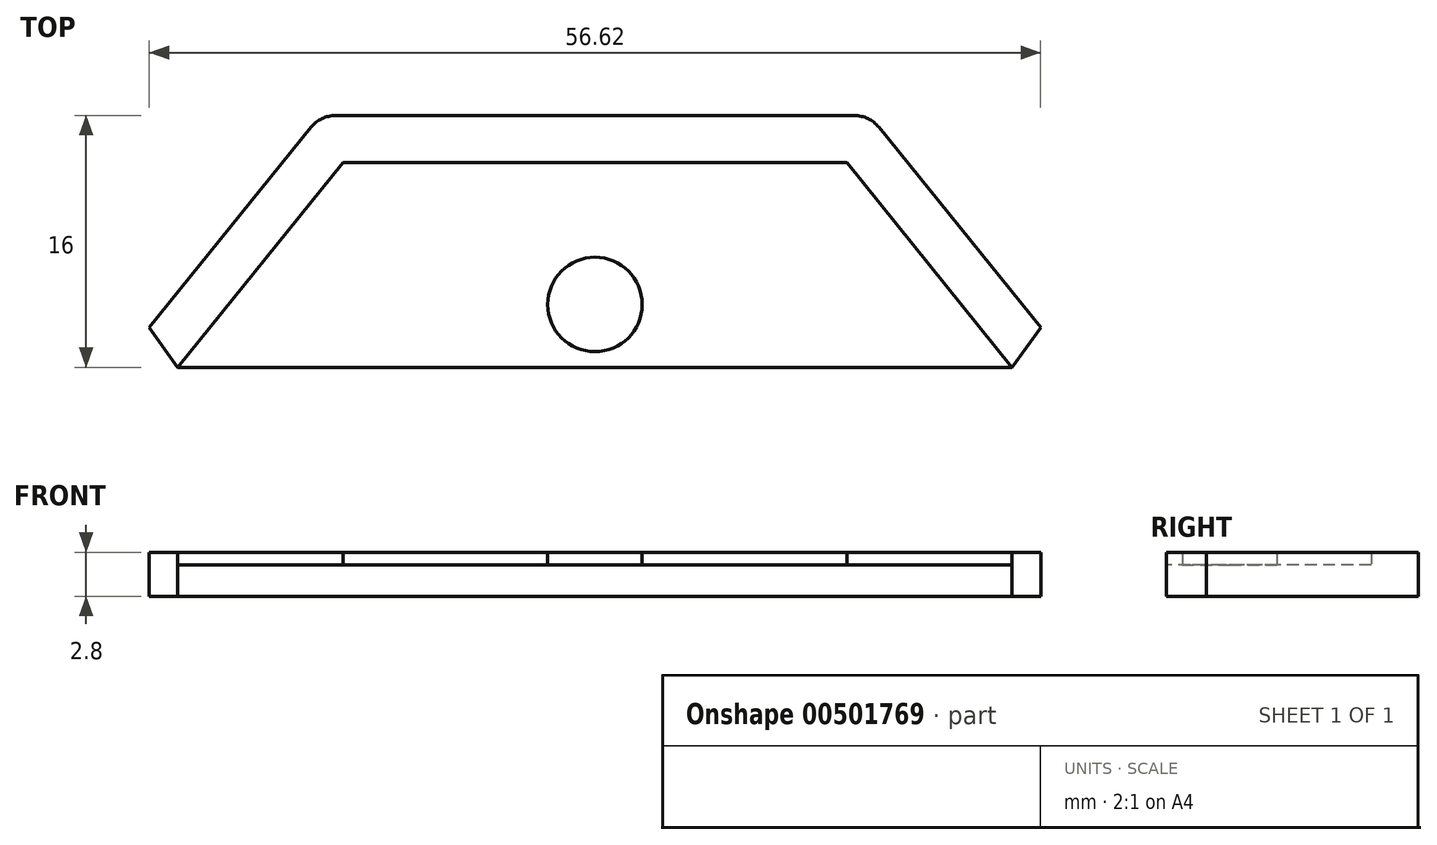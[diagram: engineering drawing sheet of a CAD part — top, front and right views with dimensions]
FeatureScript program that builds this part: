
annotation { "Feature Type Name" : "Feature", "Feature Type Description" : "" }
export const myFeature = defineFeature(function(context is Context, id is Id, definition is map)
    precondition{}
    {
        {
            var Q0;
            Q0=qCreatedBy(makeId("Top.planeOp"),FACE);
            var sketch = newSketch(context, id + "F0", { "sketchPlane" : qUnion([Q0])});
            skLineSegment(sketch, "E0", {"start": v(0, 17.14) * mm, "end": v(0, -16.93) * mm, "construction": true});
            skLineSegment(sketch, "E1", {"start": v(0, 10.35) * mm, "end": v(2, 10.35) * mm});
            skLineSegment(sketch, "E2", {"start": v(-4.02, 1.35) * mm, "end": v(4.37, 1.35) * mm, "construction": true});
            skLineSegment(sketch, "E3", {"start": v(16, 10.35) * mm, "end": v(26.5, -2.65) * mm});
            skLineSegment(sketch, "E4.0", {"start": v(18.03, 12.6) * mm, "end": v(28.31, -0.12) * mm});
            skLineSegment(sketch, "E4.1", {"start": v(0, 13.35) * mm, "end": v(16.48, 13.35) * mm});
            skLineSegment(sketch, "E5", {"start": v(26.5, -2.65) * mm, "end": v(28.31, -0.12) * mm});
            skLineSegment(sketch, "E6.trimOffspring", {"start": v(5.55, 10.35) * mm, "end": v(16, 10.35) * mm});
            skLineSegment(sketch, "E7.MirrorCS", {"start": v(0, 10.35) * mm, "end": v(-2, 10.35) * mm});
            skLineSegment(sketch, "E8.MirrorCS", {"start": v(-18.03, 12.6) * mm, "end": v(-28.31, -0.12) * mm});
            skLineSegment(sketch, "E9.MirrorCS", {"start": v(0, 13.35) * mm, "end": v(-16.48, 13.35) * mm});
            skLineSegment(sketch, "E10.MirrorCS", {"start": v(-26.5, -2.65) * mm, "end": v(-28.31, -0.12) * mm});
            skLineSegment(sketch, "E11.MirrorCS", {"start": v(-5.55, 10.35) * mm, "end": v(-16, 10.35) * mm});
            skLineSegment(sketch, "E12.MirrorCS", {"start": v(-16, 10.35) * mm, "end": v(-26.5, -2.65) * mm});
            skPoint(sketch, "E13.visualSharp", {"position": v(17.43, 13.35) * mm});
            skArc(sketch, "E13.filletArc", {"start": v(18.03, 12.6) * mm, "mid": v(17.34, 13.15) * mm, "end": v(16.48, 13.35) * mm});
            skPoint(sketch, "E14.visualSharp", {"position": v(-17.43, 13.35) * mm});
            skArc(sketch, "E14.filletArc", {"start": v(-16.48, 13.35) * mm, "mid": v(-17.34, 13.15) * mm, "end": v(-18.03, 12.6) * mm});
            skCircle(sketch, "E15", {"center": v(0, 1.35) * mm, "radius": 3 * mm});
            skLineSegment(sketch, "E16", {"start": v(-5.55, 10.35) * mm, "end": v(-2, 10.35) * mm});
            skLineSegment(sketch, "E17", {"start": v(2, 10.35) * mm, "end": v(5.55, 10.35) * mm});
            skSolve(sketch);
        }
        {
            var Q0;
            Q0=makeQuery(id+"F0.imprint","IMPRINT",FACE,{"disambiguationData":[TD([[makeQuery(id+"F0.imprint","IMPRINT",EDGE,{"derivedFrom":sQuery(id+"F0.wireOp",EDGE,"E1")}),1.0]])]});
            var Q1;
            Q1=makeQuery(id+"F0.imprint","IMPRINT",FACE,{"disambiguationData":[TD([[makeQuery(id+"F0.imprint","IMPRINT",EDGE,{"derivedFrom":sQuery(id+"F0.wireOp",EDGE,"E15")}),1.0]])]});
            extrude(context, id + "F1", {"entities" : qUnion([Q0, Q1]), "depth" : 0.8 * mm});
        }
        {
            var Q0;
            Q0=makeQuery(id+"F1.opExtrude","CAP_FACE",FACE,{"disambiguationData":[OSD([sQuery(id+"F0.wireOp",EDGE,"E1"),sQuery(id+"F0.wireOp",EDGE,"E3"),sQuery(id+"F0.wireOp",EDGE,"E4.0"),sQuery(id+"F0.wireOp",EDGE,"E4.1"),sQuery(id+"F0.wireOp",EDGE,"E5"),sQuery(id+"F0.wireOp",EDGE,"GxZ64EqV-oKiN-U5Ol-LcaG-U77pnODCQHXU"),sQuery(id+"F0.wireOp",EDGE,"qRq7fX5f-E0N0-4VJL-vaK8-IMkzgiwmWEJw"),sQuery(id+"F0.wireOp",EDGE,"lZGVzbHe-rwVR-fhwv-a2zz-uH3CmYgQQS4V"),sQuery(id+"F0.wireOp",EDGE,"E6.trimOffspring"),sQuery(id+"F0.wireOp",EDGE,"709991c2-eef9-4143-b830-e41ac9804358.filletArc"),sQuery(id+"F0.wireOp",EDGE,"4a422767-f878-4cbf-93ff-4ac4f6a52bea.filletArc"),sQuery(id+"F0.wireOp",EDGE,"396bec46-3a85-4edd-b66a-840cb310b33a0.MirrorCS"),sQuery(id+"F0.wireOp",EDGE,"E7.MirrorCS"),sQuery(id+"F0.wireOp",EDGE,"396bec46-3a85-4edd-b66a-840cb310b33a3.MirrorCS"),sQuery(id+"F0.wireOp",EDGE,"396bec46-3a85-4edd-b66a-840cb310b33a5.MirrorCS"),sQuery(id+"F0.wireOp",EDGE,"E8.MirrorCS"),sQuery(id+"F0.wireOp",EDGE,"E9.MirrorCS"),sQuery(id+"F0.wireOp",EDGE,"E10.MirrorCS"),sQuery(id+"F0.wireOp",EDGE,"E11.MirrorCS"),sQuery(id+"F0.wireOp",EDGE,"E12.MirrorCS"),sQuery(id+"F0.wireOp",EDGE,"E71.MirrorCS"),sQuery(id+"F0.wireOp",EDGE,"E72.MirrorCS"),sQuery(id+"F0.wireOp",EDGE,"E13.filletArc"),sQuery(id+"F0.wireOp",EDGE,"E14.filletArc")])],"isStart":true});
            var sketch = newSketch(context, id + "F2", { "sketchPlane" : qUnion([Q0])});
            skLineSegment(sketch, "E18", {"start": v(-28.31, 0.12) * mm, "end": v(-18.03, -12.6) * mm});
            skPoint(sketch, "E19.endSnap0", {"position": v(17.34, -13.15) * mm});
            skLineSegment(sketch, "E20", {"start": v(16.48, -13.35) * mm, "end": v(-16.48, -13.35) * mm});
            skLineSegment(sketch, "E21", {"start": v(28.31, 0.12) * mm, "end": v(18.03, -12.6) * mm});
            skPoint(sketch, "E22.orphan", {"position": v(19.51, -13.35) * mm});
            skLineSegment(sketch, "E23", {"start": v(28.31, 0.12) * mm, "end": v(26.5, 2.65) * mm});
            skLineSegment(sketch, "E24", {"start": v(26.5, 2.65) * mm, "end": v(-26.5, 2.65) * mm});
            skLineSegment(sketch, "E25", {"start": v(-26.5, 2.65) * mm, "end": v(-28.31, 0.12) * mm});
            skPoint(sketch, "E26.visualSharp", {"position": v(-17.43, -13.35) * mm});
            skArc(sketch, "E26.filletArc", {"start": v(-18.03, -12.6) * mm, "mid": v(-17.34, -13.15) * mm, "end": v(-16.48, -13.35) * mm});
            skPoint(sketch, "E27.visualSharp", {"position": v(17.43, -13.35) * mm});
            skArc(sketch, "E27.filletArc", {"start": v(16.48, -13.35) * mm, "mid": v(17.34, -13.15) * mm, "end": v(18.03, -12.6) * mm});
            skSolve(sketch);
        }
        {
            var Q0;
            Q0 = qSketchRegion(id + "F2", true);
            extrude(context, id + "F3", {"entities" : qUnion([Q0]), "operationType" : NewBodyOperationType.ADD, "depth" : 2 * mm});
        }
    });
